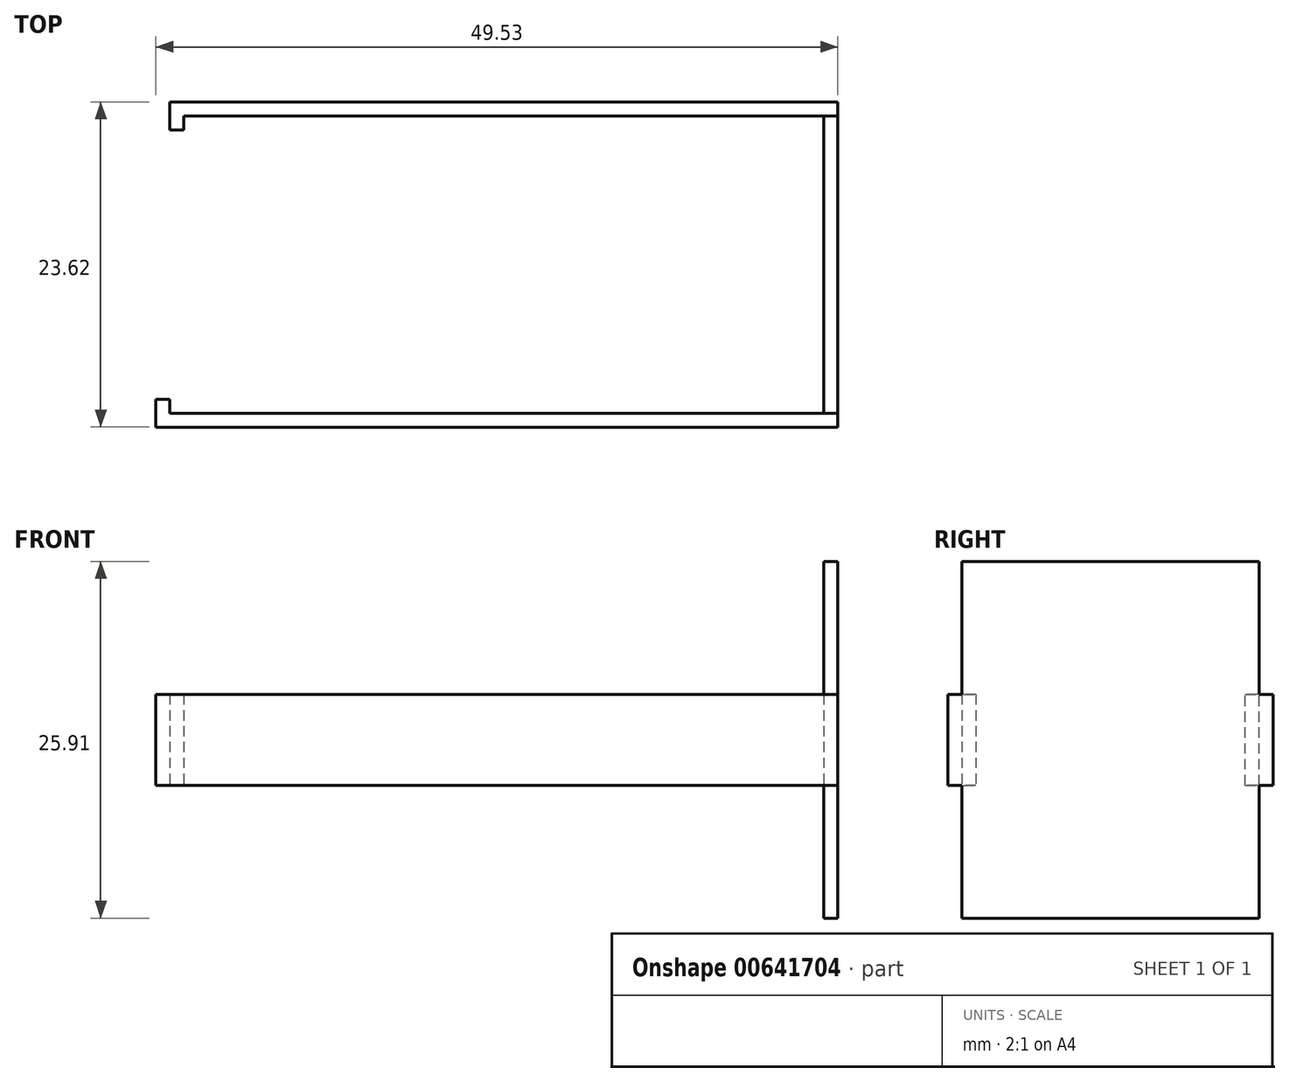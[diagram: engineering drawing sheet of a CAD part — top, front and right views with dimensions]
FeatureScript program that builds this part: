
annotation { "Feature Type Name" : "Feature", "Feature Type Description" : "" }
export const myFeature = defineFeature(function(context is Context, id is Id, definition is map)
    precondition{}
    {
        {
            var Q0;
            Q0=qCreatedBy(makeId("Front.planeOp"),FACE);
            var sketch = newSketch(context, id + "F0", { "sketchPlane" : qUnion([Q0])});
            skLineSegment(sketch, "E0.bottom", {"start": v(0, 0) * mm, "end": v(-47, 0) * mm});
            skLineSegment(sketch, "E0.top", {"start": v(0, 6.6) * mm, "end": v(-47, 6.6) * mm});
            skLineSegment(sketch, "E0.left", {"start": v(0, 0) * mm, "end": v(0, 6.6) * mm});
            skLineSegment(sketch, "E0.right", {"start": v(-47, 0) * mm, "end": v(-47, 6.6) * mm});
            skLineSegment(sketch, "E1.bottom", {"start": v(-47, 0) * mm, "end": v(-47.5, 0) * mm});
            skLineSegment(sketch, "E1.top", {"start": v(-47, 6.6) * mm, "end": v(-47.5, 6.6) * mm});
            skLineSegment(sketch, "E1.right", {"start": v(-47.5, 0) * mm, "end": v(-47.5, 6.6) * mm});
            skLineSegment(sketch, "E2.bottom", {"start": v(-47.5, 0) * mm, "end": v(-48.51, 0) * mm});
            skLineSegment(sketch, "E2.top", {"start": v(-47.5, 6.6) * mm, "end": v(-48.51, 6.6) * mm});
            skLineSegment(sketch, "E2.right", {"start": v(-48.51, 0) * mm, "end": v(-48.51, 6.6) * mm});
            skSolve(sketch);
        }
        {
            var Q0;
            Q0=makeQuery(id+"F0.imprint","IMPRINT",FACE,{"disambiguationData":[TD([[makeQuery(id+"F0.imprint","IMPRINT",EDGE,{"derivedFrom":sQuery(id+"F0.wireOp",EDGE,"E0.bottom")}),-1.0]])]});
            extrude(context, id + "F1", {"entities" : qUnion([Q0]), "depth" : 1.02 * mm});
        }
        {
            var Q0;
            Q0=makeQuery(id+"F1.opExtrude","CAP_FACE",FACE,{"disambiguationData":[OSD([sQuery(id+"F0.wireOp",EDGE,"E0.bottom"),sQuery(id+"F0.wireOp",EDGE,"E0.top"),sQuery(id+"F0.wireOp",EDGE,"E0.left"),sQuery(id+"F0.wireOp",EDGE,"E0.right")])],"isStart":false});
            var sketch = newSketch(context, id + "F2", { "sketchPlane" : qUnion([Q0])});
            skLineSegment(sketch, "E3.bottom", {"start": v(-47, 6.6) * mm, "end": v(-47.5, 6.6) * mm});
            skLineSegment(sketch, "E3.top", {"start": v(-47, 0) * mm, "end": v(-47.5, 0) * mm});
            skLineSegment(sketch, "E3.left", {"start": v(-47, 6.6) * mm, "end": v(-47, 0) * mm});
            skLineSegment(sketch, "E3.right", {"start": v(-47.5, 6.6) * mm, "end": v(-47.5, 0) * mm});
            skLineSegment(sketch, "E4.bottom", {"start": v(-47.5, 0) * mm, "end": v(-48.51, 0) * mm});
            skLineSegment(sketch, "E4.top", {"start": v(-47.5, 6.6) * mm, "end": v(-48.51, 6.6) * mm});
            skLineSegment(sketch, "E4.left", {"start": v(-47.5, 0) * mm, "end": v(-47.5, 6.6) * mm});
            skLineSegment(sketch, "E4.right", {"start": v(-48.51, 0) * mm, "end": v(-48.51, 6.6) * mm});
            skSolve(sketch);
        }
        {
            var Q0;
            Q0=makeQuery(id+"F2.imprint","IMPRINT",FACE,{"disambiguationData":[TD([[makeQuery(id+"F2.imprint","IMPRINT",EDGE,{"derivedFrom":sQuery(id+"F2.wireOp",EDGE,"E3.bottom")}),1.0]])]});
            var Q1;
            Q1=makeQuery(id+"F2.imprint","IMPRINT",FACE,{"disambiguationData":[TD([[makeQuery(id+"F2.imprint","IMPRINT",EDGE,{"derivedFrom":sQuery(id+"F2.wireOp",EDGE,"E4.bottom")}),-1.0]])]});
            extrude(context, id + "F3", {"entities" : qUnion([Q0, Q1]), "operationType" : NewBodyOperationType.ADD, "oppositeDirection" : true, "depth" : 1.02 * mm});
        }
        {
            var Q0;
            Q0=makeQuery(id+"F3.boolean.opBoolean","MERGE",FACE,{"derivedFrom":[makeQuery(id+"F1.opExtrude","CAP_FACE",FACE,{"disambiguationData":[OSD([sQuery(id+"F0.wireOp",EDGE,"E0.bottom"),sQuery(id+"F0.wireOp",EDGE,"E0.top"),sQuery(id+"F0.wireOp",EDGE,"E0.left"),sQuery(id+"F0.wireOp",EDGE,"E0.right")])],"isStart":false}),makeQuery(id+"F3.opExtrude","CAP_FACE",FACE,{"disambiguationData":[OSD([sQuery(id+"F2.wireOp",EDGE,"E3.bottom"),sQuery(id+"F2.wireOp",EDGE,"E3.top"),sQuery(id+"F2.wireOp",EDGE,"E3.left"),sQuery(id+"F2.wireOp",EDGE,"E4.bottom"),sQuery(id+"F2.wireOp",EDGE,"E4.top"),sQuery(id+"F2.wireOp",EDGE,"E4.right")])],"isStart":true})]});
            var sketch = newSketch(context, id + "F4", { "sketchPlane" : qUnion([Q0])});
            skLineSegment(sketch, "E5.bottom", {"start": v(-48.51, 6.6) * mm, "end": v(-47.5, 6.6) * mm});
            skLineSegment(sketch, "E5.top", {"start": v(-48.51, 0) * mm, "end": v(-47.5, 0) * mm});
            skLineSegment(sketch, "E5.left", {"start": v(-48.51, 6.6) * mm, "end": v(-48.51, 0) * mm});
            skLineSegment(sketch, "E5.right", {"start": v(-47.5, 6.6) * mm, "end": v(-47.5, 0) * mm});
            skSolve(sketch);
        }
        {
            var Q0;
            Q0=makeQuery(id+"F4.imprint","IMPRINT",FACE,{"disambiguationData":[TD([[makeQuery(id+"F4.imprint","IMPRINT",EDGE,{"derivedFrom":sQuery(id+"F4.wireOp",EDGE,"E5.bottom")}),1.0]])]});
            extrude(context, id + "F5", {"entities" : qUnion([Q0]), "operationType" : NewBodyOperationType.ADD, "depth" : 1.02 * mm});
        }
        {
            var Q0;
            Q0=makeQuery(id+"F3.boolean.opBoolean","MERGE",FACE,{"derivedFrom":[makeQuery(id+"F1.opExtrude","CAP_FACE",FACE,{"disambiguationData":[OSD([sQuery(id+"F0.wireOp",EDGE,"E0.bottom"),sQuery(id+"F0.wireOp",EDGE,"E0.top"),sQuery(id+"F0.wireOp",EDGE,"E0.left"),sQuery(id+"F0.wireOp",EDGE,"E0.right")])],"isStart":false}),makeQuery(id+"F3.opExtrude","CAP_FACE",FACE,{"disambiguationData":[OSD([sQuery(id+"F2.wireOp",EDGE,"E3.bottom"),sQuery(id+"F2.wireOp",EDGE,"E3.top"),sQuery(id+"F2.wireOp",EDGE,"E3.left"),sQuery(id+"F2.wireOp",EDGE,"E4.bottom"),sQuery(id+"F2.wireOp",EDGE,"E4.top"),sQuery(id+"F2.wireOp",EDGE,"E4.right")])],"isStart":true})]});
            var sketch = newSketch(context, id + "F6", { "sketchPlane" : qUnion([Q0])});
            skLineSegment(sketch, "E6.bottom", {"start": v(0, 0) * mm, "end": v(-1.02, 0) * mm});
            skLineSegment(sketch, "E6.top", {"start": v(0, 6.6) * mm, "end": v(-1.02, 6.6) * mm});
            skLineSegment(sketch, "E6.left", {"start": v(0, 0) * mm, "end": v(0, 6.6) * mm});
            skLineSegment(sketch, "E6.right", {"start": v(-1.02, 0) * mm, "end": v(-1.02, 6.6) * mm});
            skSolve(sketch);
        }
        {
            var Q0;
            Q0=makeQuery(id+"F6.imprint","IMPRINT",FACE,{"disambiguationData":[TD([[makeQuery(id+"F6.imprint","IMPRINT",EDGE,{"derivedFrom":sQuery(id+"F6.wireOp",EDGE,"E6.bottom")}),-1.0]])]});
            extrude(context, id + "F7", {"entities" : qUnion([Q0]), "operationType" : NewBodyOperationType.ADD, "depth" : 21.59 * mm});
        }
        {
            var Q0;
            Q0=makeQuery(id+"F7.opExtrude","CAP_FACE",FACE,{"disambiguationData":[OSD([sQuery(id+"F6.wireOp",EDGE,"E6.bottom"),sQuery(id+"F6.wireOp",EDGE,"E6.top"),sQuery(id+"F6.wireOp",EDGE,"E6.left"),sQuery(id+"F6.wireOp",EDGE,"E6.right")])],"isStart":false});
            extrude(context, id + "F8", {"entities" : qUnion([Q0]), "operationType" : NewBodyOperationType.ADD, "depth" : 1.02 * mm});
        }
        {
            var Q0;
            {var subQ0=sQuery(id+"F6.wireOp",EDGE,"E6.right");Q0=makeQuery(id+"F8.boolean.opBoolean","MERGE",FACE,{"derivedFrom":[makeQuery(id+"F7.opExtrude","SWEPT_FACE",FACE,{"disambiguationData":[OSD([subQ0])]}),makeQuery(id+"F8.opExtrude","SWEPT_FACE",FACE,{"disambiguationData":[OSD([subQ0])]})]});}
            var sketch = newSketch(context, id + "F9", { "sketchPlane" : qUnion([Q0])});
            skLineSegment(sketch, "E7.bottom", {"start": v(23.62, 6.6) * mm, "end": v(22.6, 6.6) * mm});
            skLineSegment(sketch, "E7.top", {"start": v(23.62, 0) * mm, "end": v(22.6, 0) * mm});
            skLineSegment(sketch, "E7.left", {"start": v(23.62, 6.6) * mm, "end": v(23.62, 0) * mm});
            skLineSegment(sketch, "E7.right", {"start": v(22.6, 6.6) * mm, "end": v(22.6, 0) * mm});
            skSolve(sketch);
        }
        {
            var Q0;
            Q0=makeQuery(id+"F9.imprint","IMPRINT",FACE,{"disambiguationData":[TD([[makeQuery(id+"F9.imprint","IMPRINT",EDGE,{"derivedFrom":sQuery(id+"F9.wireOp",EDGE,"E7.bottom")}),1.0]])]});
            extrude(context, id + "F10", {"entities" : qUnion([Q0]), "operationType" : NewBodyOperationType.ADD, "depth" : 47 * mm});
        }
        {
            var Q0;
            Q0=makeQuery(id+"F10.opExtrude","CAP_FACE",FACE,{"disambiguationData":[OSD([sQuery(id+"F9.wireOp",EDGE,"E7.bottom"),sQuery(id+"F9.wireOp",EDGE,"E7.top"),sQuery(id+"F9.wireOp",EDGE,"E7.left"),sQuery(id+"F9.wireOp",EDGE,"E7.right")])],"isStart":false});
            extrude(context, id + "F11", {"entities" : qUnion([Q0]), "operationType" : NewBodyOperationType.ADD, "depth" : 1.52 * mm});
        }
        {
            var Q0;
            {var subQ0=sQuery(id+"F9.wireOp",EDGE,"E7.right");Q0=makeQuery(id+"F11.boolean.opBoolean","MERGE",FACE,{"derivedFrom":[makeQuery(id+"F10.opExtrude","SWEPT_FACE",FACE,{"disambiguationData":[OSD([subQ0])]}),makeQuery(id+"F11.opExtrude","SWEPT_FACE",FACE,{"disambiguationData":[OSD([subQ0])]})]});}
            var sketch = newSketch(context, id + "F12", { "sketchPlane" : qUnion([Q0])});
            skLineSegment(sketch, "E8.bottom", {"start": v(49.53, 6.6) * mm, "end": v(48.51, 6.6) * mm});
            skLineSegment(sketch, "E8.top", {"start": v(49.53, 0) * mm, "end": v(48.51, 0) * mm});
            skLineSegment(sketch, "E8.left", {"start": v(49.53, 6.6) * mm, "end": v(49.53, 0) * mm});
            skLineSegment(sketch, "E8.right", {"start": v(48.51, 6.6) * mm, "end": v(48.51, 0) * mm});
            skSolve(sketch);
        }
        {
            var Q0;
            Q0=makeQuery(id+"F12.imprint","IMPRINT",FACE,{"disambiguationData":[TD([[makeQuery(id+"F12.imprint","IMPRINT",EDGE,{"derivedFrom":sQuery(id+"F12.wireOp",EDGE,"E8.bottom")}),1.0]])]});
            extrude(context, id + "F13", {"entities" : qUnion([Q0]), "operationType" : NewBodyOperationType.ADD, "depth" : 1.02 * mm});
        }
        {
            var Q0;
            {var subQ0=sQuery(id+"F9.wireOp",EDGE,"E7.bottom");var subQ1=sQuery(id+"F6.wireOp",EDGE,"E6.top");Q0=makeQuery(id+"F13.boolean.opBoolean","MERGE",FACE,{"derivedFrom":[makeQuery(id+"F11.boolean.opBoolean","MERGE",FACE,{"derivedFrom":[makeQuery(id+"F10.boolean.opBoolean","MERGE",FACE,{"derivedFrom":[makeQuery(id+"F8.boolean.opBoolean","MERGE",FACE,{"derivedFrom":[makeQuery(id+"F7.boolean.opBoolean","MERGE",FACE,{"derivedFrom":[makeQuery(id+"F5.boolean.opBoolean","MERGE",FACE,{"derivedFrom":[makeQuery(id+"F3.boolean.opBoolean","MERGE",FACE,{"derivedFrom":[makeQuery(id+"F1.opExtrude","SWEPT_FACE",FACE,{"disambiguationData":[OSD([sQuery(id+"F0.wireOp",EDGE,"E0.top")])]}),makeQuery(id+"F3.opExtrude","SWEPT_FACE",FACE,{"disambiguationData":[OSD([sQuery(id+"F2.wireOp",EDGE,"E3.bottom"),sQuery(id+"F2.wireOp",EDGE,"E4.top")])]})]}),makeQuery(id+"F5.opExtrude","SWEPT_FACE",FACE,{"disambiguationData":[OSD([sQuery(id+"F4.wireOp",EDGE,"E5.bottom")])]})]}),makeQuery(id+"F7.opExtrude","SWEPT_FACE",FACE,{"disambiguationData":[OSD([subQ1])]})]}),makeQuery(id+"F8.opExtrude","SWEPT_FACE",FACE,{"disambiguationData":[OSD([subQ1])]})]}),makeQuery(id+"F10.opExtrude","SWEPT_FACE",FACE,{"disambiguationData":[OSD([subQ0])]})]}),makeQuery(id+"F11.opExtrude","SWEPT_FACE",FACE,{"disambiguationData":[OSD([subQ0])]})]}),makeQuery(id+"F13.opExtrude","SWEPT_FACE",FACE,{"disambiguationData":[OSD([sQuery(id+"F12.wireOp",EDGE,"E8.bottom")])]})]});}
            var sketch = newSketch(context, id + "F14", { "sketchPlane" : qUnion([Q0])});
            skLineSegment(sketch, "E9.bottom", {"start": v(-1.02, -1.02) * mm, "end": v(0, -1.02) * mm});
            skLineSegment(sketch, "E9.top", {"start": v(-1.02, -22.6) * mm, "end": v(0, -22.6) * mm});
            skLineSegment(sketch, "E9.left", {"start": v(-1.02, -1.02) * mm, "end": v(-1.02, -22.6) * mm});
            skLineSegment(sketch, "E9.right", {"start": v(0, -1.02) * mm, "end": v(0, -22.6) * mm});
            skSolve(sketch);
        }
        {
            var Q0;
            {var subQ0=sQuery(id+"F6.wireOp",EDGE,"E6.right");Q0=makeQuery(id+"F8.boolean.opBoolean","MERGE",FACE,{"derivedFrom":[makeQuery(id+"F7.opExtrude","SWEPT_FACE",FACE,{"disambiguationData":[OSD([subQ0])]}),makeQuery(id+"F8.opExtrude","SWEPT_FACE",FACE,{"disambiguationData":[OSD([subQ0])]})]});}
            var sketch = newSketch(context, id + "F15", { "sketchPlane" : qUnion([Q0])});
            skSolve(sketch);
        }
        {
            var Q0;
            Q0=qSketchRegion(id+"F15",true);
            var Q1;
            Q1=makeQuery(id+"F14.imprint","IMPRINT",FACE,{"disambiguationData":[TD([[makeQuery(id+"F14.imprint","IMPRINT",EDGE,{"derivedFrom":sQuery(id+"F14.wireOp",EDGE,"E9.bottom")}),-1.0]])]});
            extrude(context, id + "F16", {"entities" : qUnion([Q0, Q1]), "operationType" : NewBodyOperationType.ADD, "depth" : 9.65 * mm});
        }
        {
            var Q0;
            {var subQ0=sQuery(id+"F9.wireOp",EDGE,"E7.top");var subQ1=sQuery(id+"F6.wireOp",EDGE,"E6.bottom");Q0=makeQuery(id+"F13.boolean.opBoolean","MERGE",FACE,{"derivedFrom":[makeQuery(id+"F11.boolean.opBoolean","MERGE",FACE,{"derivedFrom":[makeQuery(id+"F10.boolean.opBoolean","MERGE",FACE,{"derivedFrom":[makeQuery(id+"F8.boolean.opBoolean","MERGE",FACE,{"derivedFrom":[makeQuery(id+"F7.boolean.opBoolean","MERGE",FACE,{"derivedFrom":[makeQuery(id+"F5.boolean.opBoolean","MERGE",FACE,{"derivedFrom":[makeQuery(id+"F3.boolean.opBoolean","MERGE",FACE,{"derivedFrom":[makeQuery(id+"F1.opExtrude","SWEPT_FACE",FACE,{"disambiguationData":[OSD([sQuery(id+"F0.wireOp",EDGE,"E0.bottom")])]}),makeQuery(id+"F3.opExtrude","SWEPT_FACE",FACE,{"disambiguationData":[OSD([sQuery(id+"F2.wireOp",EDGE,"E3.top"),sQuery(id+"F2.wireOp",EDGE,"E4.bottom")])]})]}),makeQuery(id+"F5.opExtrude","SWEPT_FACE",FACE,{"disambiguationData":[OSD([sQuery(id+"F4.wireOp",EDGE,"E5.top")])]})]}),makeQuery(id+"F7.opExtrude","SWEPT_FACE",FACE,{"disambiguationData":[OSD([subQ1])]})]}),makeQuery(id+"F8.opExtrude","SWEPT_FACE",FACE,{"disambiguationData":[OSD([subQ1])]})]}),makeQuery(id+"F10.opExtrude","SWEPT_FACE",FACE,{"disambiguationData":[OSD([subQ0])]})]}),makeQuery(id+"F11.opExtrude","SWEPT_FACE",FACE,{"disambiguationData":[OSD([subQ0])]})]}),makeQuery(id+"F13.opExtrude","SWEPT_FACE",FACE,{"disambiguationData":[OSD([sQuery(id+"F12.wireOp",EDGE,"E8.top")])]})]});}
            var sketch = newSketch(context, id + "F17", { "sketchPlane" : qUnion([Q0])});
            skLineSegment(sketch, "E10.bottom", {"start": v(-1.02, 1.02) * mm, "end": v(0, 1.02) * mm});
            skLineSegment(sketch, "E10.top", {"start": v(-1.02, 22.6) * mm, "end": v(0, 22.6) * mm});
            skLineSegment(sketch, "E10.left", {"start": v(-1.02, 1.02) * mm, "end": v(-1.02, 22.6) * mm});
            skLineSegment(sketch, "E10.right", {"start": v(0, 1.02) * mm, "end": v(0, 22.6) * mm});
            skSolve(sketch);
        }
        {
            var Q0;
            Q0=makeQuery(id+"F17.imprint","IMPRINT",FACE,{"disambiguationData":[TD([[makeQuery(id+"F17.imprint","IMPRINT",EDGE,{"derivedFrom":sQuery(id+"F17.wireOp",EDGE,"E10.bottom")}),1.0]])]});
            extrude(context, id + "F18", {"entities" : qUnion([Q0]), "operationType" : NewBodyOperationType.ADD, "depth" : 9.65 * mm});
        }
    });
